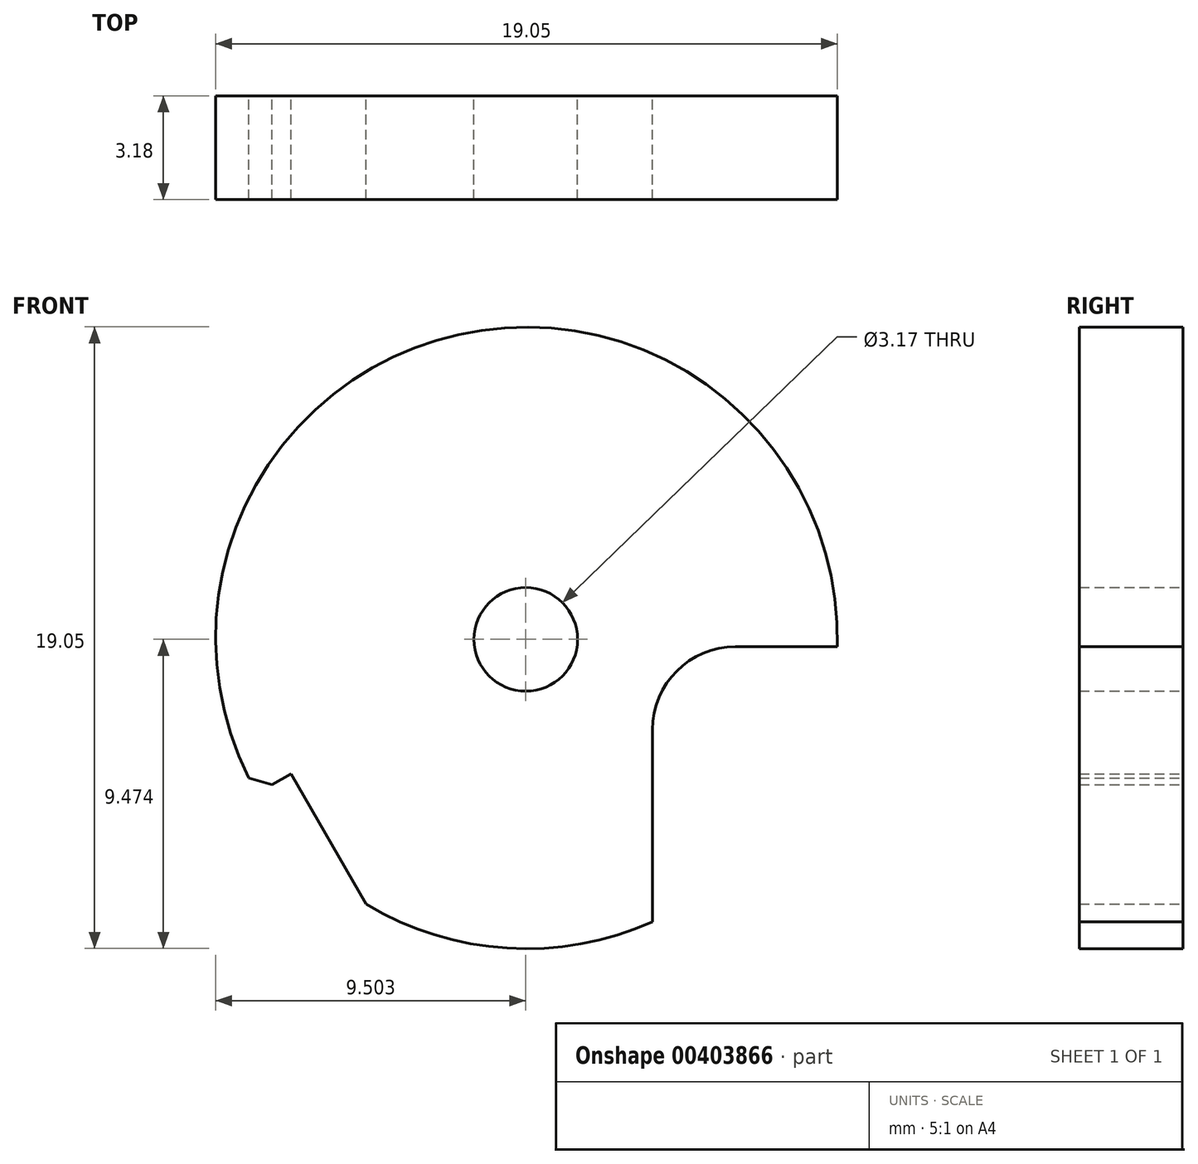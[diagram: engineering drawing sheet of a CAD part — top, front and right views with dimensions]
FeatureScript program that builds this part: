
annotation { "Feature Type Name" : "Feature", "Feature Type Description" : "" }
export const myFeature = defineFeature(function(context is Context, id is Id, definition is map)
    precondition{}
    {
        {
            var Q0;
            Q0=qCreatedBy(makeId("Front.planeOp"),FACE);
            var sketch = newSketch(context, id + "F0", { "sketchPlane" : qUnion([Q0])});
            skCircle(sketch, "E0", {"center": v(-0.15, 2.73) * mm, "radius": 1.59 * mm});
            skArc(sketch, "E1", {"start": v(6.28, 2.5) * mm, "mid": v(4.48, 1.76) * mm, "end": v(3.74, -0.03) * mm});
            skLineSegment(sketch, "E2", {"start": v(3.74, -5.93) * mm, "end": v(3.74, -0.03) * mm});
            skLineSegment(sketch, "E3", {"start": v(6.28, 2.5) * mm, "end": v(9.4, 2.5) * mm});
            skLineSegment(sketch, "E4", {"start": v(-7.34, -1.39) * mm, "end": v(-5.04, -5.38) * mm});
            skLineSegment(sketch, "E5.trimOffspring", {"start": v(-7.34, -1.39) * mm, "end": v(-8.38, -1.98) * mm});
            skArc(sketch, "E6", {"start": v(-5.04, -5.38) * mm, "mid": v(-0.72, -6.73) * mm, "end": v(3.74, -5.93) * mm});
            skArc(sketch, "E7", {"start": v(9.4, 2.5) * mm, "mid": v(-2.46, 12.02) * mm, "end": v(-8.38, -1.98) * mm});
            skSolve(sketch);
        }
        {
            var Q0;
            Q0=makeQuery(id+"F0.imprint","IMPRINT",FACE,{"disambiguationData":[TD([[makeQuery(id+"F0.imprint","IMPRINT",EDGE,{"derivedFrom":sQuery(id+"F0.wireOp",EDGE,"E0")}),-1.0]])]});
            extrude(context, id + "F1", {"entities" : qUnion([Q0]), "endBound" : BoundingType.SYMMETRIC, "depth" : 3.17 * mm});
        }
        {
            var Q0;
            Q0=makeQuery(id+"F1.opExtrude","SWEPT_EDGE",EDGE,{"disambiguationData":[OSD([sQuery(id+"F0.wireOp",EDGE,"E5.trimOffspring"),sQuery(id+"F0.wireOp",EDGE,"E7")])]});
            chamfer(context, id + "F2", {"entities" : qUnion([Q0]), "width" : 0.5 * mm, "tangentPropagation" : true});
        }
    });
